# Revit family: Novojunta Pro Aluminio PLUS SP
name_source: partatom
category: Modelos genéricos
units: mm (PartAtom-declared; Revit-internal decimal feet)

## family parameters
Compartido = No
Corte con vacíos al cargar = No
Cota de conector redondo = Usar diámetro
Mantener orientación de anotación = No
Puede alojar armadura = No
Punto de cálculo de habitación = No
Tipo de pieza = Normal

## types (1)
- Novojunta Pro Aluminio PLUS SP
    Descripción = NOVOJUNTA PRO ALUMINIO PLUS SP
    Elevación por defecto = 0 mm  [stored 0 ft]
    Texto Descriptivo = Novojunta® Pro Aluminio PLUS SP es un sistema de perfiles de aluminio reforzados y caucho EPDM destinado a  colocación en juntas de dilatación de estructura superpuestas de hasta 50 mm de ancho. Su diseño facilita la absorción de los movimientos derivados de las variaciones térmicas, permitiendo movimiento en tres ejes.  Con acabado liso o estriado y soporte de cargas medias. Se sirve desmontada. Disponible en color gris o negro.

note: [stored X ft] marks values corroborated as IEEE doubles in the binary element streams (Revit-internal decimal feet)

## geometry (parser evidence)
native form markers: Sweep x9
no freeform markers — native parametric forms only
